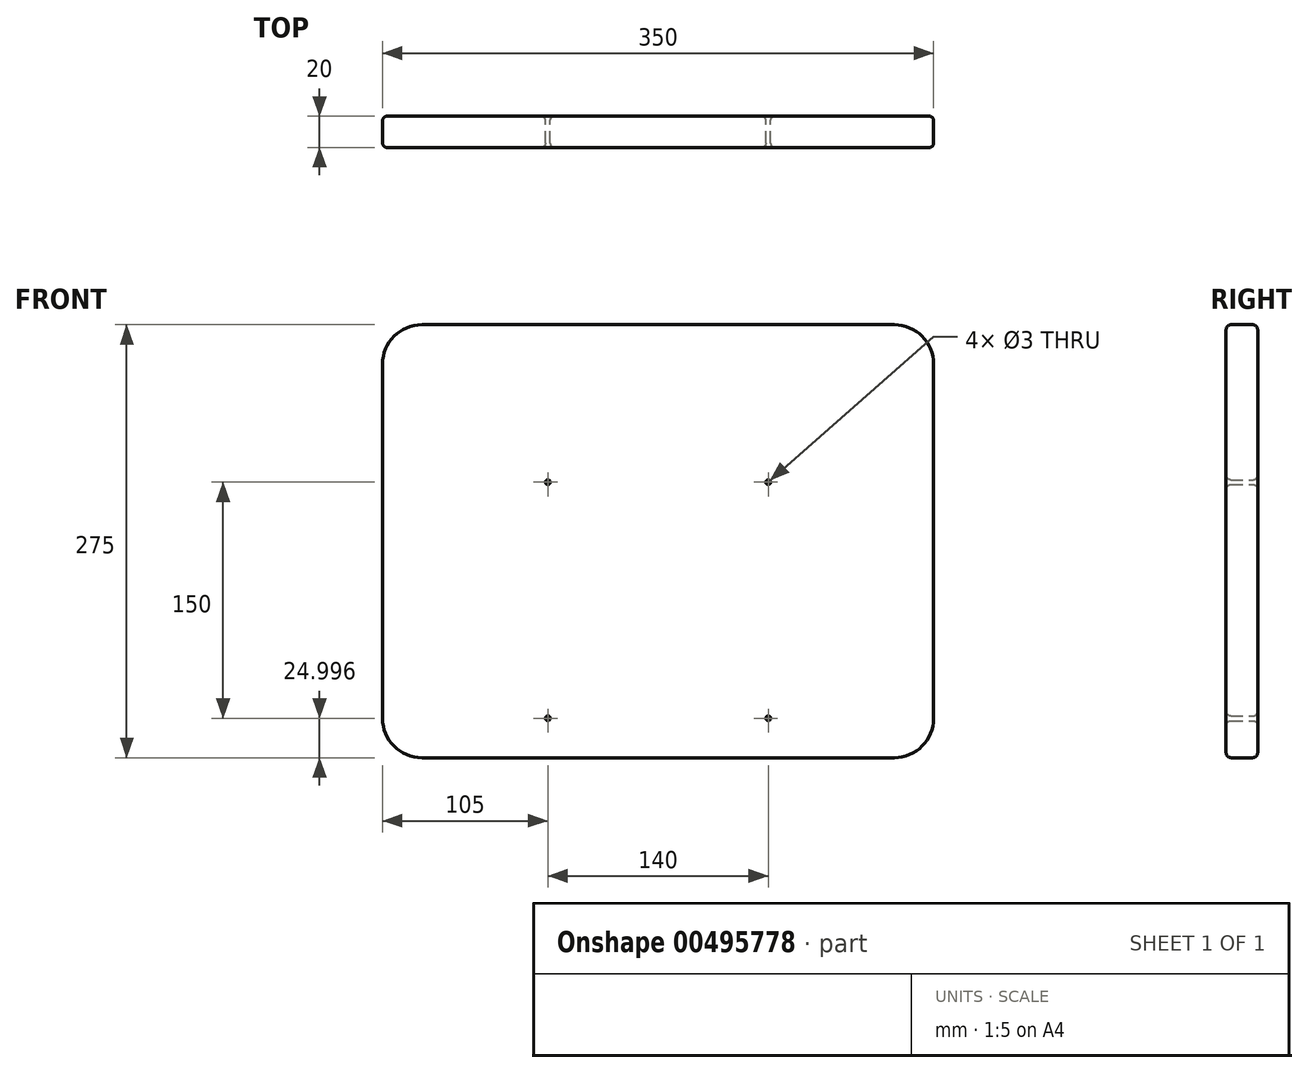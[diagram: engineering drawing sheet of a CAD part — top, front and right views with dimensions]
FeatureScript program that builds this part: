
annotation { "Feature Type Name" : "Feature", "Feature Type Description" : "" }
export const myFeature = defineFeature(function(context is Context, id is Id, definition is map)
    precondition{}
    {
        {
            var Q0;
            Q0=qCreatedBy(makeId("Front.planeOp"),FACE);
            var sketch = newSketch(context, id + "F0", { "sketchPlane" : qUnion([Q0])});
            skPoint(sketch, "E0", {"position": v(0, 74.27) * mm});
            skLineSegment(sketch, "E1", {"start": v(0, 74.27) * mm, "end": v(0, 24.04) * mm});
            skLineSegment(sketch, "E2", {"start": v(0, 174.27) * mm, "end": v(-150, 174.27) * mm});
            skLineSegment(sketch, "E3", {"start": v(-175, 149.27) * mm, "end": v(-175, 24.27) * mm});
            skLineSegment(sketch, "E4", {"start": v(-150, -100.73) * mm, "end": v(0, -100.73) * mm});
            skLineSegment(sketch, "E5", {"start": v(-175, 24.27) * mm, "end": v(-175, -75.73) * mm});
            skPoint(sketch, "E6.visualSharp", {"position": v(-175, 174.27) * mm});
            skArc(sketch, "E6.filletArc", {"start": v(-150, 174.27) * mm, "mid": v(-167.68, 166.94) * mm, "end": v(-175, 149.27) * mm});
            skPoint(sketch, "E7.visualSharp", {"position": v(-175, -100.73) * mm});
            skArc(sketch, "E7.filletArc", {"start": v(-175, -75.73) * mm, "mid": v(-167.68, -93.41) * mm, "end": v(-150, -100.73) * mm});
            skCircle(sketch, "E8", {"center": v(-70, 74.27) * mm, "radius": 1.5 * mm});
            skCircle(sketch, "E9", {"center": v(-70, -75.73) * mm, "radius": 1.5 * mm});
            skLineSegment(sketch, "E10.MirrorCS", {"start": v(0, 174.27) * mm, "end": v(150, 174.27) * mm});
            skArc(sketch, "E11.MirrorCS", {"start": v(150, 174.27) * mm, "mid": v(167.68, 166.94) * mm, "end": v(175, 149.27) * mm});
            skLineSegment(sketch, "E12.MirrorCS", {"start": v(175, 149.27) * mm, "end": v(175, 24.27) * mm});
            skArc(sketch, "E13.MirrorCS", {"start": v(175, -75.73) * mm, "mid": v(167.68, -93.41) * mm, "end": v(150, -100.73) * mm});
            skLineSegment(sketch, "E14.MirrorCS", {"start": v(150, -100.73) * mm, "end": v(0, -100.73) * mm});
            skLineSegment(sketch, "E15.MirrorCS", {"start": v(175, 24.27) * mm, "end": v(175, -75.73) * mm});
            skCircle(sketch, "E16.MirrorC", {"center": v(70, 74.27) * mm, "radius": 1.5 * mm});
            skCircle(sketch, "E17.MirrorC", {"center": v(70, -75.73) * mm, "radius": 1.5 * mm});
            skLineSegment(sketch, "E18", {"start": v(0, 74.27) * mm, "end": v(0, -82.47) * mm});
            skLineSegment(sketch, "E19", {"start": v(0, -82.47) * mm, "end": v(0, 86.66) * mm});
            skLineSegment(sketch, "E20", {"start": v(-70, 74.27) * mm, "end": v(0, 74.27) * mm});
            skLineSegment(sketch, "E21", {"start": v(0, 74.27) * mm, "end": v(70, 74.27) * mm});
            skLineSegment(sketch, "E22", {"start": v(70, -75.73) * mm, "end": v(0, -75.73) * mm});
            skLineSegment(sketch, "E23", {"start": v(0, -75.73) * mm, "end": v(-70, -75.73) * mm});
            skLineSegment(sketch, "E24", {"start": v(-70, -75.73) * mm, "end": v(-70, -100.73) * mm});
            skSolve(sketch);
        }
        {
            var Q0;
            Q0=makeQuery(id+"F0.imprint","IMPRINT",FACE,{"disambiguationData":[TD([[makeQuery(id+"F0.imprint","IMPRINT",EDGE,{"derivedFrom":sQuery(id+"F0.wireOp",EDGE,"E2")}),1.0]])]});
            extrude(context, id + "F1", {"entities" : qUnion([Q0]), "endBound" : BoundingType.SYMMETRIC, "depth" : 20 * mm});
        }
        {
            var Q0;
            Q0=makeQuery(id+"F1.opExtrude","CAP_FACE",FACE,{"disambiguationData":[OSD([sQuery(id+"F0.wireOp",EDGE,"E2"),sQuery(id+"F0.wireOp",EDGE,"E3"),sQuery(id+"F0.wireOp",EDGE,"E4"),sQuery(id+"F0.wireOp",EDGE,"E5"),sQuery(id+"F0.wireOp",EDGE,"E6.filletArc"),sQuery(id+"F0.wireOp",EDGE,"E7.filletArc"),sQuery(id+"F0.wireOp",EDGE,"E8"),sQuery(id+"F0.wireOp",EDGE,"E9"),sQuery(id+"F0.wireOp",EDGE,"E10.MirrorCS"),sQuery(id+"F0.wireOp",EDGE,"E11.MirrorCS"),sQuery(id+"F0.wireOp",EDGE,"E12.MirrorCS"),sQuery(id+"F0.wireOp",EDGE,"E13.MirrorCS"),sQuery(id+"F0.wireOp",EDGE,"E14.MirrorCS"),sQuery(id+"F0.wireOp",EDGE,"E15.MirrorCS"),sQuery(id+"F0.wireOp",EDGE,"E16.MirrorC"),sQuery(id+"F0.wireOp",EDGE,"E17.MirrorC")])],"isStart":true});
            var Q1;
            Q1=makeQuery(id+"F1.opExtrude","CAP_FACE",FACE,{"disambiguationData":[OSD([sQuery(id+"F0.wireOp",EDGE,"E2"),sQuery(id+"F0.wireOp",EDGE,"E3"),sQuery(id+"F0.wireOp",EDGE,"E4"),sQuery(id+"F0.wireOp",EDGE,"E5"),sQuery(id+"F0.wireOp",EDGE,"E6.filletArc"),sQuery(id+"F0.wireOp",EDGE,"E7.filletArc"),sQuery(id+"F0.wireOp",EDGE,"E8"),sQuery(id+"F0.wireOp",EDGE,"E9"),sQuery(id+"F0.wireOp",EDGE,"E10.MirrorCS"),sQuery(id+"F0.wireOp",EDGE,"E11.MirrorCS"),sQuery(id+"F0.wireOp",EDGE,"E12.MirrorCS"),sQuery(id+"F0.wireOp",EDGE,"E13.MirrorCS"),sQuery(id+"F0.wireOp",EDGE,"E14.MirrorCS"),sQuery(id+"F0.wireOp",EDGE,"E15.MirrorCS"),sQuery(id+"F0.wireOp",EDGE,"E16.MirrorC"),sQuery(id+"F0.wireOp",EDGE,"E17.MirrorC")])],"isStart":false});
            fillet(context, id + "F2", {"entities" : qUnion([Q0, Q1]), "radius" : 3 * mm, "tangentPropagation" : true, "allowEdgeOverflow" : false});
        }
    });
